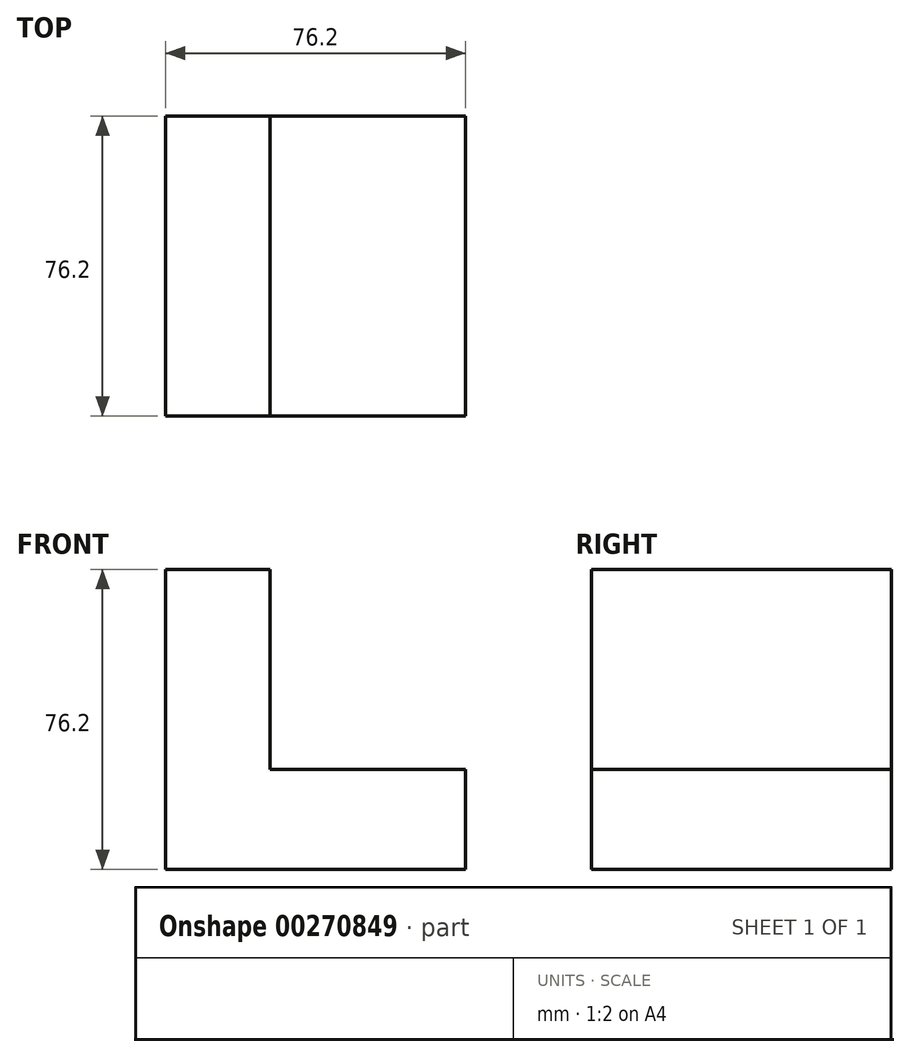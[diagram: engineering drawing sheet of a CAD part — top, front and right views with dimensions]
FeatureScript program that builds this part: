
annotation { "Feature Type Name" : "Feature", "Feature Type Description" : "" }
export const myFeature = defineFeature(function(context is Context, id is Id, definition is map)
    precondition{}
    {
        {
            var Q0;
            Q0=qCreatedBy(makeId("Front.planeOp"),FACE);
            var sketch = newSketch(context, id + "F0", { "sketchPlane" : qUnion([Q0])});
            skLineSegment(sketch, "E0", {"start": v(-67.03, 70.45) * mm, "end": v(-67.03, -5.75) * mm});
            skLineSegment(sketch, "E1", {"start": v(-67.03, -5.75) * mm, "end": v(9.17, -5.75) * mm});
            skLineSegment(sketch, "E2", {"start": v(9.17, -5.75) * mm, "end": v(9.17, 19.65) * mm});
            skLineSegment(sketch, "E3", {"start": v(-67.27, 70.45) * mm, "end": v(-41.87, 70.45) * mm});
            skLineSegment(sketch, "E4", {"start": v(9.17, 19.65) * mm, "end": v(-40.42, 19.65) * mm});
            skLineSegment(sketch, "E5", {"start": v(-40.42, 19.65) * mm, "end": v(-40.42, 70.45) * mm});
            skLineSegment(sketch, "E6", {"start": v(-41.87, 70.45) * mm, "end": v(-40.42, 70.45) * mm});
            skSolve(sketch);
        }
        {
            var Q0;
            {var subQ1=sQuery(id+"F0.wireOp",EDGE,"E0");Q0=makeQuery(id+"F0.imprint","IMPRINT",FACE,{"disambiguationData":[TD([[makeQuery(id+"F0.imprint","IMPRINT",EDGE,{"derivedFrom":subQ1}),1.0]])]});}
            extrude(context, id + "F1", {"entities" : qUnion([Q0]), "depth" : 76.2 * mm});
        }
    });
